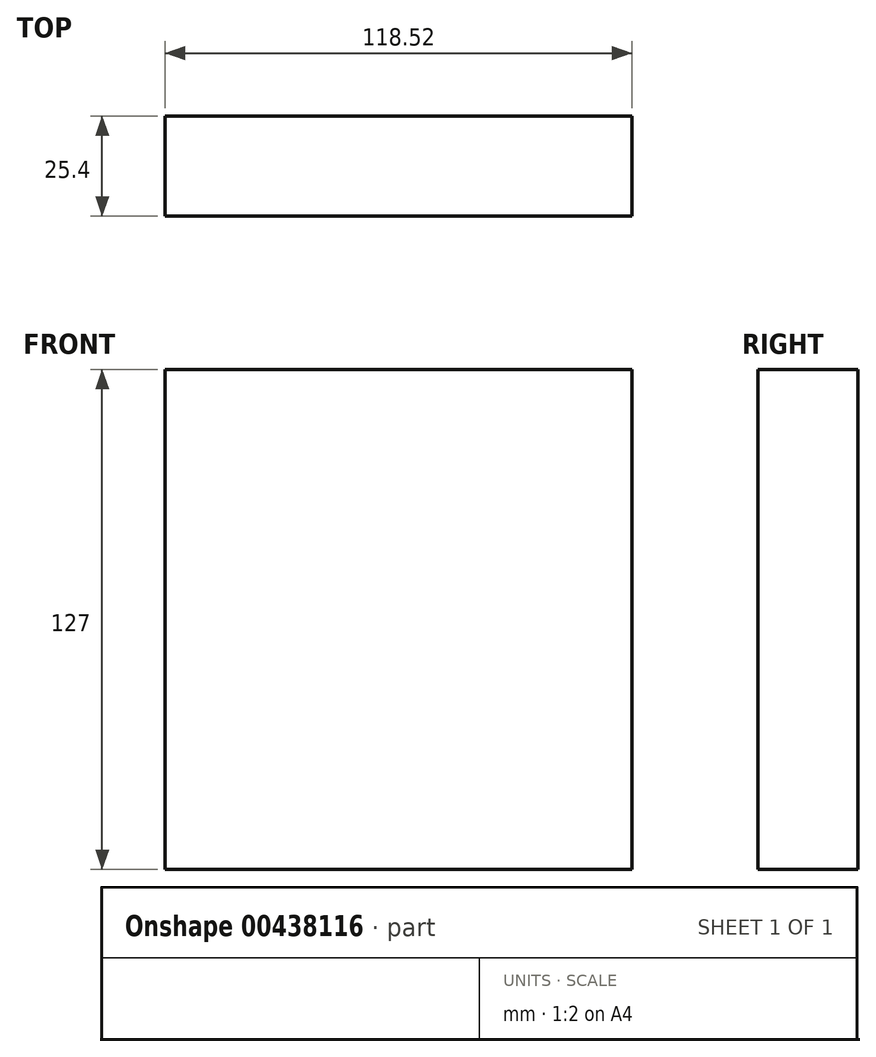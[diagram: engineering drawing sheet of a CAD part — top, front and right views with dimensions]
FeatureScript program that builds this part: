
annotation { "Feature Type Name" : "Feature", "Feature Type Description" : "" }
export const myFeature = defineFeature(function(context is Context, id is Id, definition is map)
    precondition{}
    {
        {
            var Q0;
            Q0=qCreatedBy(makeId("Front.planeOp"),FACE);
            var sketch = newSketch(context, id + "F0", { "sketchPlane" : qUnion([Q0])});
            skLineSegment(sketch, "E0.bottom", {"start": v(-54.27, 114.03) * mm, "end": v(64.25, 114.03) * mm});
            skLineSegment(sketch, "E0.top", {"start": v(-54.27, -12.97) * mm, "end": v(64.25, -12.97) * mm});
            skLineSegment(sketch, "E0.left", {"start": v(-54.27, 114.03) * mm, "end": v(-54.27, -12.97) * mm});
            skLineSegment(sketch, "E0.right", {"start": v(64.25, 114.03) * mm, "end": v(64.25, -12.97) * mm});
            skSolve(sketch);
        }
        {
            var Q0;
            Q0=makeQuery(id+"F0.imprint","IMPRINT",FACE,{"disambiguationData":[TD([[makeQuery(id+"F0.imprint","IMPRINT",EDGE,{"derivedFrom":sQuery(id+"F0.wireOp",EDGE,"E0.bottom")}),-1.0]])]});
            extrude(context, id + "F1", {"entities" : qUnion([Q0]), "depth" : 25.4 * mm, "offsetDistance" : 25.4 * mm});
        }
    });
